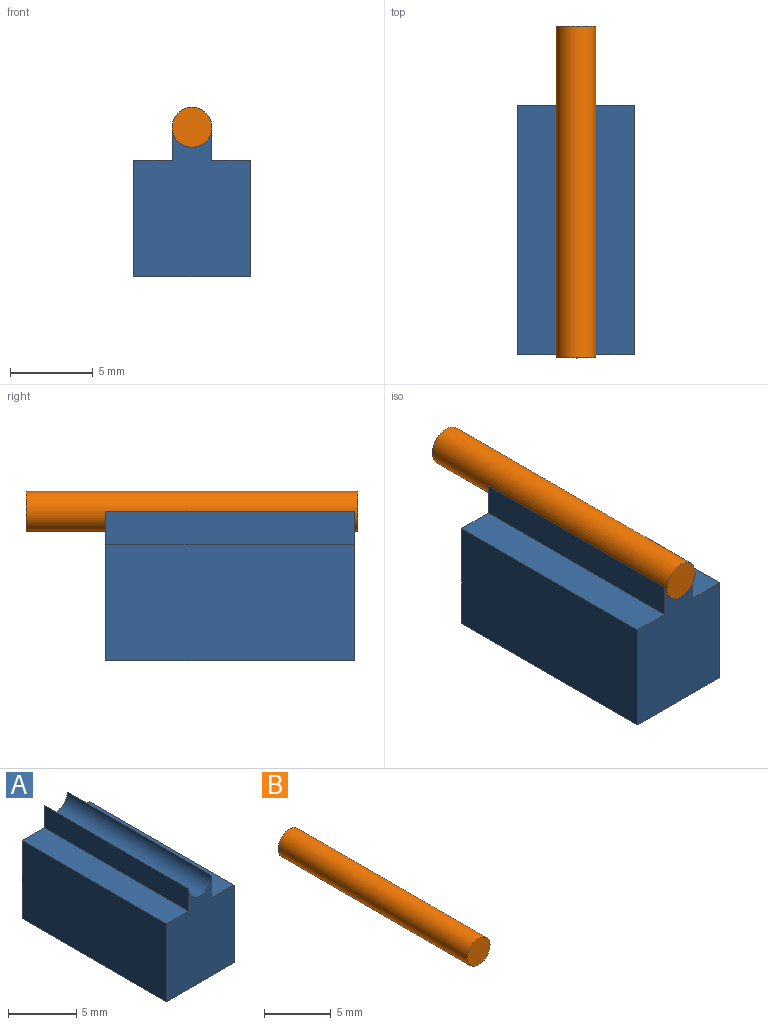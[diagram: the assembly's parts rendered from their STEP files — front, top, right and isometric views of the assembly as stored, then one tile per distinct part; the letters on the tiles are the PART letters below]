
ASSEMBLY  parts=2 mates=1
PART A: 10 faces, bbox 7x15x9 mm
  f0: plane 15x7mm, normal (-1,0,0), area 105mm2, adj f1,f7,f8,f9
  f1: plane 15x7mm, normal (0,0,-1), area 105mm2, adj f0,f2,f8,f9
  f2: plane 15x7mm, normal (1,0,0), area 105mm2, adj f1,f3,f8,f9
  f3: plane 15x2.3mm, normal (0,0,1), area 34.5mm2, adj f2,f4,f8,f9
  f4: plane 15x2mm, normal (1,0,0), area 30mm2, adj f3,f5,f8,f9
  f5: cylinder r=1.2mm len=15mm, axis (0,1,0), area 56.5mm2, adj f4,f6,f8,f9
  f6: plane 15x2mm, normal (-1,0,0), area 30mm2, adj f5,f7,f8,f9
  f7: plane 15x2.3mm, normal (0,0,1), area 34.5mm2, adj f0,f6,f8,f9
  f8: plane 9x7mm, normal (0,-1,0), area 51.5mm2, adj f0,f1,f2,f3,f4,f5,f6,f7
  f9: plane 9x7mm, normal (0,1,0), area 51.5mm2, adj f0,f1,f2,f3,f4,f5,f6,f7
PART B: 3 faces, bbox 2.4x20x2.4 mm
  f0: cylinder r=1.2mm len=20mm, axis (0,1,0), area 150.8mm2, adj f1,f2
  f1: plane 2.4x2.4mm, normal (0,-1,0), area 4.5mm2, adj f0
  f2: plane 2.4x2.4mm, normal (0,1,0), area 4.5mm2, adj f0
PLACE A at identity fixed
PLACE B t=(-0.52,4.8,-12.65)mm
MATE fastened B.f0 <-> A.f5  axis (0,1,0) through (-0.52,-5.2,-12.65)mm
